# Revit family: f5fd465b-0319-4c63-bc98-8e1c0b9e7d54
name_source: partatom
category: Furniture
revit_build: Autodesk Revit 2016 (Build: 20161004_0715(x64)
units: mm (PartAtom-declared; Revit-internal decimal feet)

## family parameters
Cut with Voids When Loaded = No
Host = Face
OmniClass Number = 23.40.95.00
OmniClass Title = Furnishings, Ornaments, and Decoration
Room Calculation Point = No
Shared = No

## types (1)
- 54"
    Assembly Code = E2010
    Default Elevation = 54"
    Depth = 5"
    Description = Ligature Resistant Protective TV Enclosure
    Frame Finish = Aluminum-BSP-Anodized-Black
    Front Protection Finish = Polycarbonate-BSP-Clear
    Height = 36"
    Inset Finish = Plastic-BSP-Black
    Load Classification = Other
    Manufacturer = Behavioral Safety Products
    Model = TE540
    Notes = Fabrication to client specifications
    Options = Includes Ligature Resistant Slope
    Product Documentation Link = http://besafeprod.com
    Product Page URL = http://besafeprod.com
    Product data url = https://bimobject.com
    Show Ligature Resistant Slope = Yes
    Type Image = <None>
    URL = http://besafeprod.com
    Use Charger = No
    Use USB = Yes
    Voltage = 5 V
    Width = 48"

## geometry (parser evidence)
native form markers: Blend x8, Sweep x2
no freeform markers — native parametric forms only
